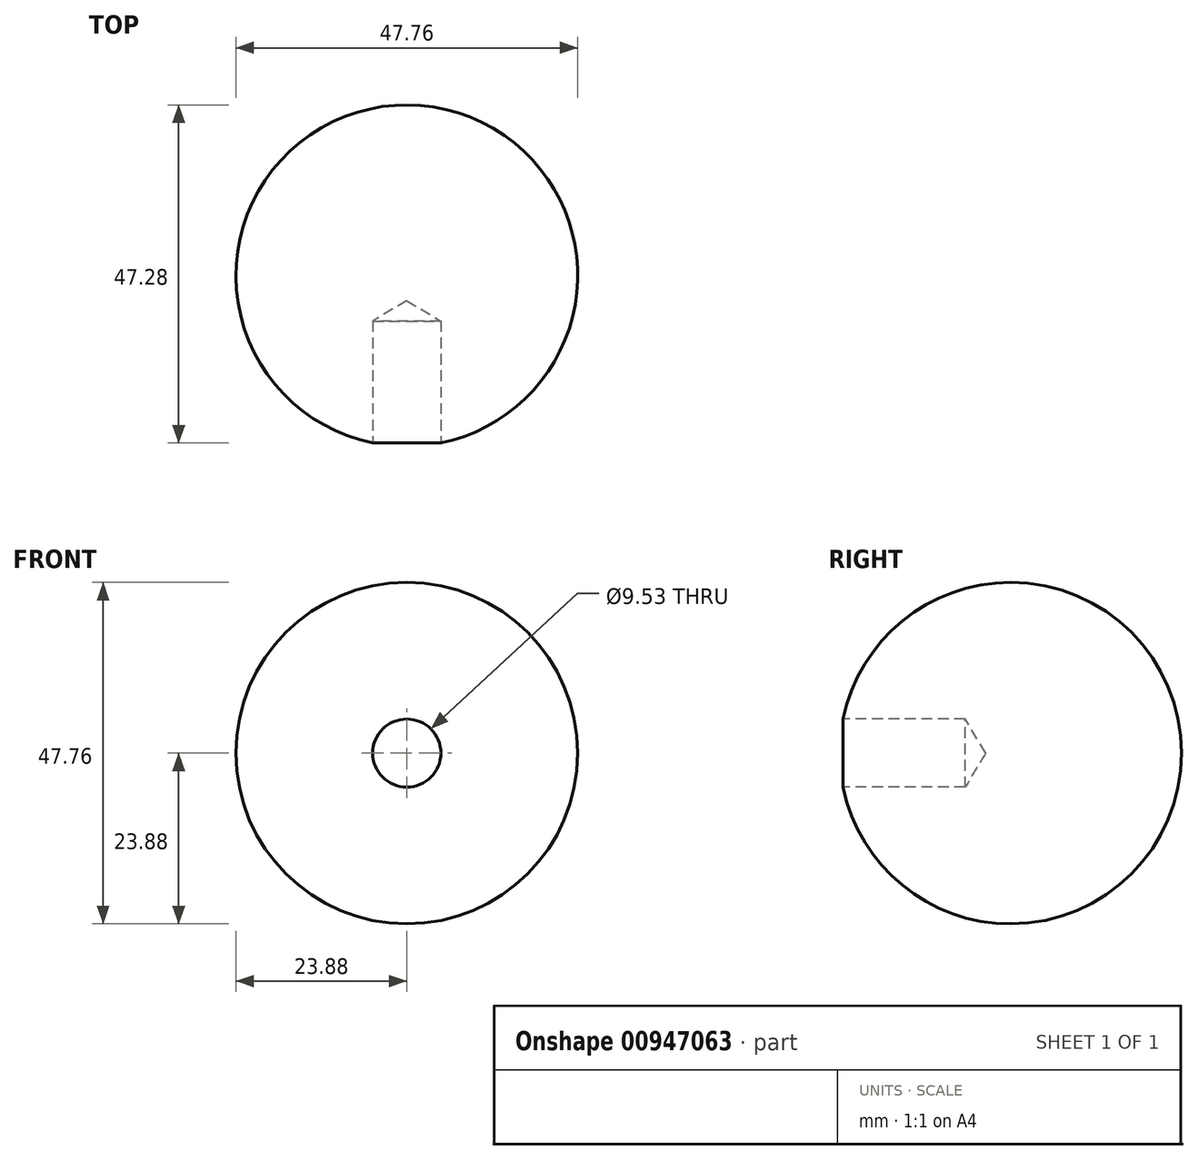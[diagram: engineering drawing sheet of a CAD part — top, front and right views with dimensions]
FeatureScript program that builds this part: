
annotation { "Feature Type Name" : "Feature", "Feature Type Description" : "" }
export const myFeature = defineFeature(function(context is Context, id is Id, definition is map)
    precondition{}
    {
        {
            var Q0;
            Q0=qCreatedBy(makeId("Front.planeOp"),FACE);
            var sketch = newSketch(context, id + "F0", { "sketchPlane" : qUnion([Q0])});
            skArc(sketch, "E0", {"start": v(0, -23.88) * mm, "mid": v(23.88, 0) * mm, "end": v(0, 23.88) * mm});
            skLineSegment(sketch, "E1", {"start": v(0, 0) * mm, "end": v(23.88, 0) * mm, "construction": true});
            skLineSegment(sketch, "E2", {"start": v(0, 23.88) * mm, "end": v(0, -23.88) * mm});
            skSolve(sketch);
        }
        {
            var Q0;
            Q0=qSketchRegion(id+"F0",true);
            var Q1;
            Q1=sQuery(id+"F0.wireOp",EDGE,"E2");
            revolve(context, id + "F1", {"surfaceOperationType" : NewSurfaceOperationType.NEW, "entities" : qUnion([Q0]), "axis" : qUnion([Q1]), "revolveType" : RevolveType.FULL});
        }
        {
            var Q0;
            Q0=qCreatedBy(makeId("Front.planeOp"),FACE);
            cPlane(context, id + "F2", {"entities" : qUnion([Q0]), "cplaneType" : CPlaneType.OFFSET, "offset" : 25.4 * mm, "width" : 152.4 * mm, "height" : 152.4 * mm});
        }
        {
            var Q0;
            Q0=qCreatedBy(id+"F2.planeOp",FACE);
            var sketch = newSketch(context, id + "F3", { "sketchPlane" : qUnion([Q0])});
            skPoint(sketch, "E3", {"position": v(0, 0) * mm});
            skSolve(sketch);
        }
        {
            var Q0;
            Q0=sQuery(id+"F3.wireOp",VERTEX,"E3");
            var Q1;
            Q1=makeQuery(id+"F1.opRevolve","SWEPT_BODY",BODY,{"disambiguationData":[OSD([sQuery(id+"F0.wireOp",EDGE,"E0"),sQuery(id+"F0.wireOp",EDGE,"E2")])]});
            hole(context, id + "F4", {"style" : HoleStyle.SIMPLE, "endStyle" : HoleEndStyle.BLIND, "holeDiameter" : 9.52 * mm, "majorDiameter" : 6.35 * mm, "holeDepth" : 19.05 * mm, "isTappedThrough" : true, "tappedDepth" : 12.7 * mm, "tapClearance" : 3, "startFromSketch" : true, "locations" : qUnion([Q0]), "scope" : qUnion([Q1])});
        }
    });
